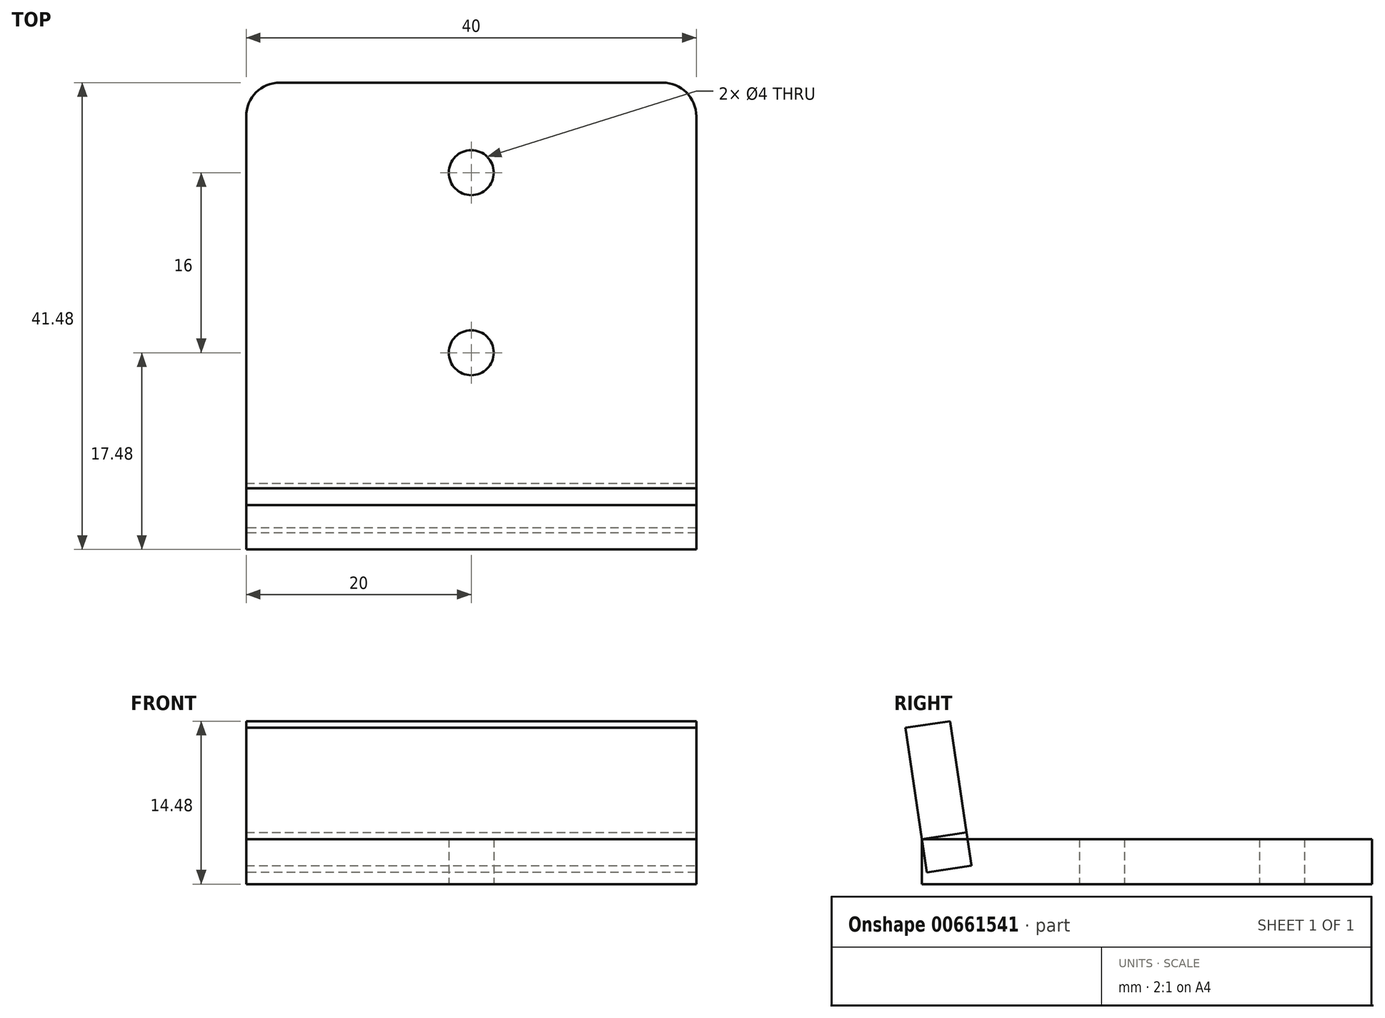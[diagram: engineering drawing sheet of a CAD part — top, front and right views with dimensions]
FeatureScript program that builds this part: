
annotation { "Feature Type Name" : "Feature", "Feature Type Description" : "" }
export const myFeature = defineFeature(function(context is Context, id is Id, definition is map)
    precondition{}
    {
        {
            var Q0;
            Q0=qCreatedBy(makeId("Top.planeOp"),FACE);
            var sketch = newSketch(context, id + "F0", { "sketchPlane" : qUnion([Q0])});
            skLineSegment(sketch, "E0", {"start": v(3, 0) * mm, "end": v(37, 0) * mm});
            skLineSegment(sketch, "E1", {"start": v(40, -3) * mm, "end": v(40, -40) * mm});
            skLineSegment(sketch, "E2", {"start": v(40, -40) * mm, "end": v(0, -40) * mm});
            skLineSegment(sketch, "E3", {"start": v(0, -40) * mm, "end": v(0, -3) * mm});
            skLineSegment(sketch, "E4", {"start": v(20, 0) * mm, "end": v(20, -8) * mm});
            skLineSegment(sketch, "E5", {"start": v(20, -40) * mm, "end": v(20, -24) * mm});
            skCircle(sketch, "E6", {"center": v(20, -8) * mm, "radius": 2 * mm});
            skCircle(sketch, "E7", {"center": v(20, -24) * mm, "radius": 2 * mm});
            skPoint(sketch, "E8.visualSharp", {"position": v(0, 0) * mm});
            skArc(sketch, "E8.filletArc", {"start": v(3, 0) * mm, "mid": v(0.88, -0.88) * mm, "end": v(0, -3) * mm});
            skPoint(sketch, "E9.visualSharp", {"position": v(40, 0) * mm});
            skArc(sketch, "E9.filletArc", {"start": v(40, -3) * mm, "mid": v(39.12, -0.88) * mm, "end": v(37, 0) * mm});
            skSolve(sketch);
        }
        {
            var Q0;
            {var subQ1=sQuery(id+"F0.wireOp",EDGE,"E1");Q0=makeQuery(id+"F0.imprint","IMPRINT",FACE,{"disambiguationData":[TD([[makeQuery(id+"F0.imprint","IMPRINT",EDGE,{"derivedFrom":subQ1}),-1.0]])]});}
            extrude(context, id + "F1", {"entities" : qUnion([Q0]), "depth" : 4 * mm, "offsetDistance" : 25 * mm});
        }
        {
            var Q0;
            Q0=makeQuery(id+"F1.opExtrude","CAP_FACE",FACE,{"disambiguationData":[OSD([sQuery(id+"F0.wireOp",EDGE,"E0"),sQuery(id+"F0.wireOp",EDGE,"E1"),sQuery(id+"F0.wireOp",EDGE,"E2"),sQuery(id+"F0.wireOp",EDGE,"E3"),sQuery(id+"F0.wireOp",EDGE,"E6"),sQuery(id+"F0.wireOp",EDGE,"E7"),sQuery(id+"F0.wireOp",EDGE,"E8.filletArc"),sQuery(id+"F0.wireOp",EDGE,"E9.filletArc")])],"isStart":false});
            var Q1;
            Q1=makeQuery(id+"F1.opExtrude","CAP_EDGE",EDGE,{"disambiguationData":[OSD([sQuery(id+"F0.wireOp",EDGE,"E2")])],"isStart":false});
            cPlane(context, id + "F2", {"entities" : qUnion([Q0, Q1]), "cplaneType" : CPlaneType.LINE_ANGLE, "offset" : 25 * mm, "angle" : 188.5 * degree, "oppositeDirection" : true, "width" : 150 * mm, "height" : 150 * mm});
        }
        {
            var Q0;
            Q0=qCreatedBy(id+"F2.planeOp",FACE);
            var sketch = newSketch(context, id + "F3", { "sketchPlane" : qUnion([Q0])});
            skLineSegment(sketch, "E10", {"start": v(40, -38.97) * mm, "end": v(0, -38.97) * mm});
            skLineSegment(sketch, "E11", {"start": v(0, -38.97) * mm, "end": v(0, -34.97) * mm});
            skLineSegment(sketch, "E12", {"start": v(0, -34.97) * mm, "end": v(40, -34.97) * mm});
            skLineSegment(sketch, "E13", {"start": v(40, -34.97) * mm, "end": v(40, -38.97) * mm});
            skSolve(sketch);
        }
        {
            var Q0;
            Q0=makeQuery(id+"F3.imprint","IMPRINT",FACE,{"disambiguationData":[TD([[makeQuery(id+"F3.imprint","IMPRINT",EDGE,{"derivedFrom":sQuery(id+"F3.wireOp",EDGE,"E10")}),-1.0]])]});
            extrude(context, id + "F4", {"entities" : qUnion([Q0]), "depth" : 10 * mm, "offsetDistance" : 25 * mm});
        }
        {
            var Q0;
            Q0=makeQuery(id+"F4.opExtrude","CAP_FACE",FACE,{"disambiguationData":[OSD([sQuery(id+"F3.wireOp",EDGE,"E10"),sQuery(id+"F3.wireOp",EDGE,"E11"),sQuery(id+"F3.wireOp",EDGE,"E12"),sQuery(id+"F3.wireOp",EDGE,"E13")])],"isStart":true});
            extrude(context, id + "F5", {"entities" : qUnion([Q0]), "depth" : 3 * mm, "offsetDistance" : 25 * mm});
        }
    });
